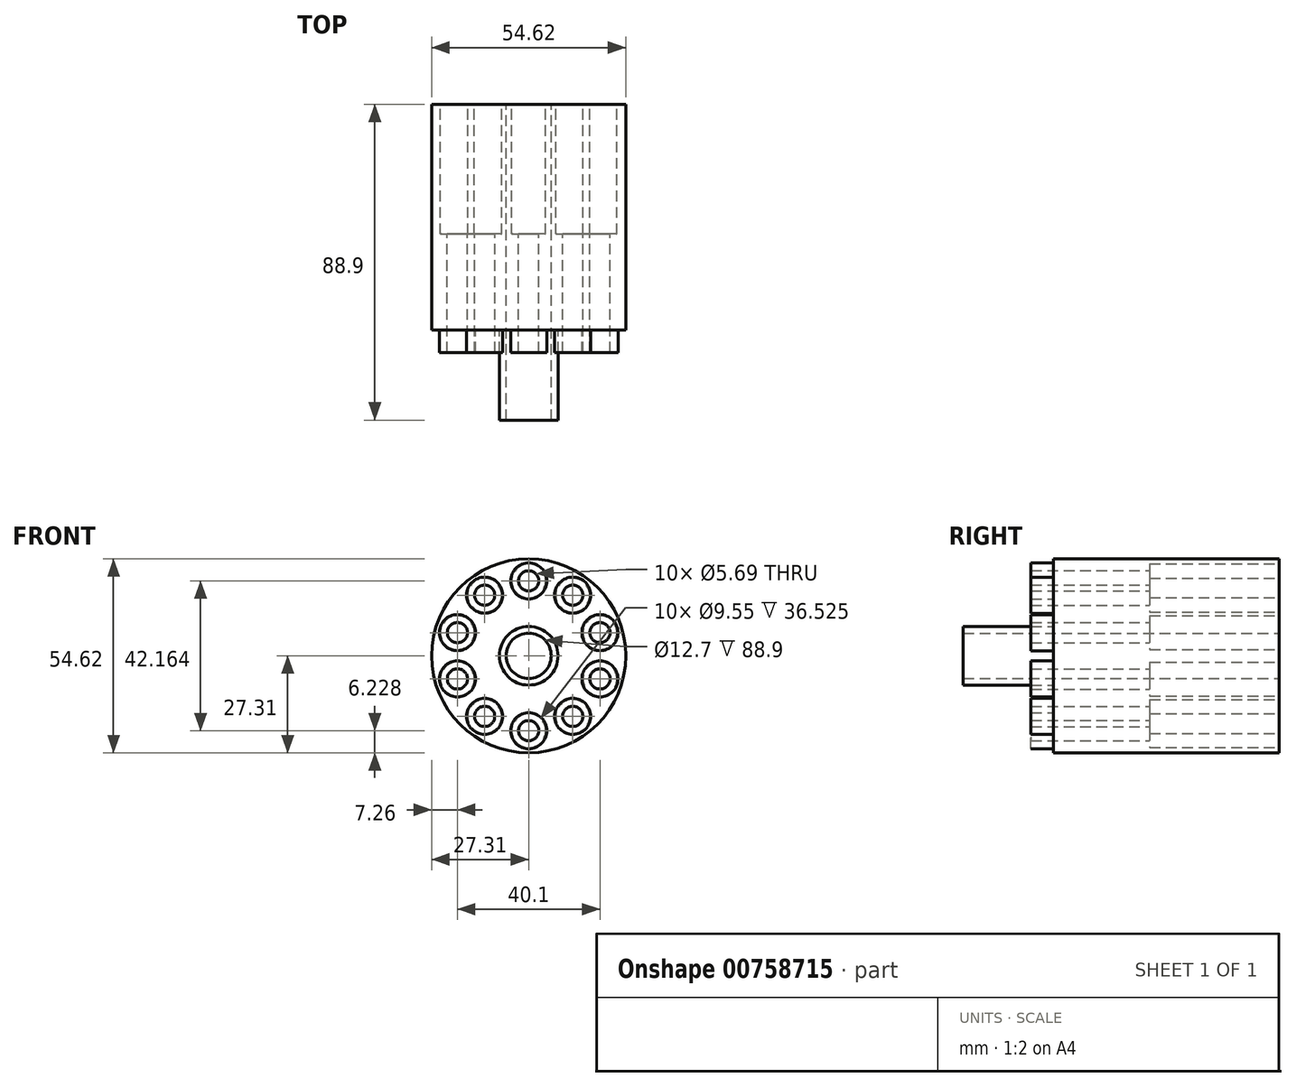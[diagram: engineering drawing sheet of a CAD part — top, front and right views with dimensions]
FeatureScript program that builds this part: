
annotation { "Feature Type Name" : "Feature", "Feature Type Description" : "" }
export const myFeature = defineFeature(function(context is Context, id is Id, definition is map)
    precondition{}
    {
        {
            var Q0;
            Q0=qCreatedBy(makeId("Front.planeOp"),FACE);
            var sketch = newSketch(context, id + "F0", { "sketchPlane" : qUnion([Q0])});
            skCircle(sketch, "E0", {"center": v(0, 0) * mm, "radius": 27.3 * mm});
            skSolve(sketch);
        }
        {
            var Q0;
            Q0 = qSketchRegion(id + "F0", true);
            extrude(context, id + "F1", {"entities" : qUnion([Q0]), "depth" : 63.5 * mm, "offsetDistance" : 25.4 * mm});
        }
        {
            var Q0;
            Q0=makeQuery(id+"F1.opExtrude","CAP_FACE",FACE,{"disambiguationData":[OSD([sQuery(id+"F0.wireOp",EDGE,"E0")])],"isStart":true});
            var sketch = newSketch(context, id + "F2", { "sketchPlane" : qUnion([Q0])});
            skLineSegment(sketch, "E1", {"start": v(0, 0) * mm, "end": v(0, 21.08) * mm});
            skLineSegment(sketch, "E2", {"start": v(0, 0) * mm, "end": v(12.4, 17.06) * mm});
            skLineSegment(sketch, "E3", {"start": v(0, 0) * mm, "end": v(20.05, 6.51) * mm});
            skLineSegment(sketch, "E4", {"start": v(0, 0) * mm, "end": v(20.05, -6.51) * mm});
            skLineSegment(sketch, "E5", {"start": v(0, 0) * mm, "end": v(12.4, -17.06) * mm});
            skLineSegment(sketch, "E6", {"start": v(0, 0) * mm, "end": v(0, -21.08) * mm});
            skLineSegment(sketch, "E7", {"start": v(0, 0) * mm, "end": v(-20.05, -6.51) * mm});
            skLineSegment(sketch, "E8", {"start": v(0, 0) * mm, "end": v(-20.05, 6.51) * mm});
            skLineSegment(sketch, "E9", {"start": v(0, 0) * mm, "end": v(-12.4, 17.06) * mm});
            skLineSegment(sketch, "E10", {"start": v(0, 0) * mm, "end": v(-12.4, -17.06) * mm});
            skCircle(sketch, "E11", {"center": v(0, 21.08) * mm, "radius": 4.78 * mm});
            skCircle(sketch, "E12", {"center": v(12.4, 17.06) * mm, "radius": 4.78 * mm});
            skCircle(sketch, "E13", {"center": v(20.05, 6.51) * mm, "radius": 4.78 * mm});
            skCircle(sketch, "E14", {"center": v(20.05, -6.51) * mm, "radius": 4.78 * mm});
            skCircle(sketch, "E15", {"center": v(12.4, -17.06) * mm, "radius": 4.78 * mm});
            skCircle(sketch, "E16", {"center": v(0, -21.08) * mm, "radius": 4.78 * mm});
            skCircle(sketch, "E17", {"center": v(-12.4, -17.06) * mm, "radius": 4.78 * mm});
            skCircle(sketch, "E18", {"center": v(-20.05, -6.51) * mm, "radius": 4.78 * mm});
            skCircle(sketch, "E19", {"center": v(-20.05, 6.51) * mm, "radius": 4.78 * mm});
            skCircle(sketch, "E20", {"center": v(-12.4, 17.06) * mm, "radius": 4.78 * mm});
            skCircle(sketch, "E21", {"center": v(0, 21.08) * mm, "radius": 2.84 * mm});
            skCircle(sketch, "E22", {"center": v(12.4, 17.06) * mm, "radius": 2.84 * mm});
            skCircle(sketch, "E23", {"center": v(20.05, 6.51) * mm, "radius": 2.84 * mm});
            skCircle(sketch, "E24", {"center": v(20.05, -6.51) * mm, "radius": 2.84 * mm});
            skCircle(sketch, "E25", {"center": v(12.4, -17.06) * mm, "radius": 2.84 * mm});
            skCircle(sketch, "E26", {"center": v(0, -21.08) * mm, "radius": 2.84 * mm});
            skCircle(sketch, "E27", {"center": v(-12.4, -17.06) * mm, "radius": 2.84 * mm});
            skCircle(sketch, "E28", {"center": v(-20.05, -6.51) * mm, "radius": 2.84 * mm});
            skCircle(sketch, "E29", {"center": v(-20.05, 6.51) * mm, "radius": 2.84 * mm});
            skCircle(sketch, "E30", {"center": v(-12.4, 17.06) * mm, "radius": 2.84 * mm});
            skSolve(sketch);
        }
        {
            var Q0;
            Q0=makeQuery(id+"F2.imprint","IMPRINT",FACE,{"disambiguationData":[TD([[makeQuery(id+"F2.imprint","IMPRINT",EDGE,{"derivedFrom":sQuery(id+"F2.wireOp",EDGE,"E28")}),1.0]])]});
            var Q1;
            Q1=makeQuery(id+"F2.imprint","IMPRINT",FACE,{"disambiguationData":[TD([[makeQuery(id+"F2.imprint","IMPRINT",EDGE,{"derivedFrom":sQuery(id+"F2.wireOp",EDGE,"E29")}),1.0]])]});
            var Q2;
            Q2=makeQuery(id+"F2.imprint","IMPRINT",FACE,{"disambiguationData":[TD([[makeQuery(id+"F2.imprint","IMPRINT",EDGE,{"derivedFrom":sQuery(id+"F2.wireOp",EDGE,"E30")}),1.0]])]});
            var Q3;
            Q3=makeQuery(id+"F2.imprint","IMPRINT",FACE,{"disambiguationData":[TD([[makeQuery(id+"F2.imprint","IMPRINT",EDGE,{"derivedFrom":sQuery(id+"F2.wireOp",EDGE,"E21")}),1.0]])]});
            var Q4;
            Q4=makeQuery(id+"F2.imprint","IMPRINT",FACE,{"disambiguationData":[TD([[makeQuery(id+"F2.imprint","IMPRINT",EDGE,{"derivedFrom":sQuery(id+"F2.wireOp",EDGE,"E22")}),1.0]])]});
            var Q5;
            Q5=makeQuery(id+"F2.imprint","IMPRINT",FACE,{"disambiguationData":[TD([[makeQuery(id+"F2.imprint","IMPRINT",EDGE,{"derivedFrom":sQuery(id+"F2.wireOp",EDGE,"E23")}),1.0]])]});
            var Q6;
            Q6=makeQuery(id+"F2.imprint","IMPRINT",FACE,{"disambiguationData":[TD([[makeQuery(id+"F2.imprint","IMPRINT",EDGE,{"derivedFrom":sQuery(id+"F2.wireOp",EDGE,"E24")}),1.0]])]});
            var Q7;
            Q7=makeQuery(id+"F2.imprint","IMPRINT",FACE,{"disambiguationData":[TD([[makeQuery(id+"F2.imprint","IMPRINT",EDGE,{"derivedFrom":sQuery(id+"F2.wireOp",EDGE,"E25")}),1.0]])]});
            var Q8;
            Q8=makeQuery(id+"F2.imprint","IMPRINT",FACE,{"disambiguationData":[TD([[makeQuery(id+"F2.imprint","IMPRINT",EDGE,{"derivedFrom":sQuery(id+"F2.wireOp",EDGE,"E26")}),1.0]])]});
            var Q9;
            Q9=makeQuery(id+"F2.imprint","IMPRINT",FACE,{"disambiguationData":[TD([[makeQuery(id+"F2.imprint","IMPRINT",EDGE,{"derivedFrom":sQuery(id+"F2.wireOp",EDGE,"E27")}),1.0]])]});
            extrude(context, id + "F3", {"entities" : qUnion([Q0, Q1, Q2, Q3, Q4, Q5, Q6, Q7, Q8, Q9]), "operationType" : NewBodyOperationType.REMOVE, "oppositeDirection" : true, "depth" : 86.61 * mm, "offsetDistance" : 25.4 * mm});
        }
        {
            var Q0;
            Q0=makeQuery(id+"F1.opExtrude","CAP_FACE",FACE,{"disambiguationData":[OSD([sQuery(id+"F0.wireOp",EDGE,"E0")])],"isStart":false});
            var sketch = newSketch(context, id + "F4", { "sketchPlane" : qUnion([Q0])});
            skCircle(sketch, "E31", {"center": v(-12.4, 17.06) * mm, "radius": 5.08 * mm});
            skCircle(sketch, "E32", {"center": v(0, 21.08) * mm, "radius": 5.08 * mm});
            skCircle(sketch, "E33", {"center": v(12.4, 17.06) * mm, "radius": 5.08 * mm});
            skCircle(sketch, "E34", {"center": v(20.05, 6.51) * mm, "radius": 5.08 * mm});
            skCircle(sketch, "E35", {"center": v(20.05, -6.51) * mm, "radius": 5.08 * mm});
            skCircle(sketch, "E36", {"center": v(12.4, -17.06) * mm, "radius": 5.08 * mm});
            skCircle(sketch, "E37", {"center": v(0, -21.08) * mm, "radius": 5.08 * mm});
            skCircle(sketch, "E38", {"center": v(-12.4, -17.06) * mm, "radius": 5.08 * mm});
            skCircle(sketch, "E39", {"center": v(-20.05, -6.51) * mm, "radius": 5.08 * mm});
            skCircle(sketch, "E40", {"center": v(-20.05, 6.51) * mm, "radius": 5.08 * mm});
            skSolve(sketch);
        }
        {
            var Q0;
            Q0=makeQuery(id+"F4.imprint","IMPRINT",FACE,{"disambiguationData":[TD([[makeQuery(id+"F4.imprint","IMPRINT",EDGE,{"derivedFrom":sQuery(id+"F4.wireOp",EDGE,"E32")}),1.0]])]});
            var Q1;
            Q1=makeQuery(id+"F4.imprint","IMPRINT",FACE,{"disambiguationData":[TD([[makeQuery(id+"F4.imprint","IMPRINT",EDGE,{"derivedFrom":sQuery(id+"F4.wireOp",EDGE,"E33")}),1.0]])]});
            var Q2;
            Q2=makeQuery(id+"F4.imprint","IMPRINT",FACE,{"disambiguationData":[TD([[makeQuery(id+"F4.imprint","IMPRINT",EDGE,{"derivedFrom":sQuery(id+"F4.wireOp",EDGE,"E34")}),1.0]])]});
            var Q3;
            Q3=makeQuery(id+"F4.imprint","IMPRINT",FACE,{"disambiguationData":[TD([[makeQuery(id+"F4.imprint","IMPRINT",EDGE,{"derivedFrom":sQuery(id+"F4.wireOp",EDGE,"E35")}),1.0]])]});
            var Q4;
            Q4=makeQuery(id+"F4.imprint","IMPRINT",FACE,{"disambiguationData":[TD([[makeQuery(id+"F4.imprint","IMPRINT",EDGE,{"derivedFrom":sQuery(id+"F4.wireOp",EDGE,"E36")}),1.0]])]});
            var Q5;
            Q5=makeQuery(id+"F4.imprint","IMPRINT",FACE,{"disambiguationData":[TD([[makeQuery(id+"F4.imprint","IMPRINT",EDGE,{"derivedFrom":sQuery(id+"F4.wireOp",EDGE,"E37")}),1.0]])]});
            var Q6;
            Q6=makeQuery(id+"F4.imprint","IMPRINT",FACE,{"disambiguationData":[TD([[makeQuery(id+"F4.imprint","IMPRINT",EDGE,{"derivedFrom":sQuery(id+"F4.wireOp",EDGE,"E38")}),1.0]])]});
            var Q7;
            Q7=makeQuery(id+"F4.imprint","IMPRINT",FACE,{"disambiguationData":[TD([[makeQuery(id+"F4.imprint","IMPRINT",EDGE,{"derivedFrom":sQuery(id+"F4.wireOp",EDGE,"E39")}),1.0]])]});
            var Q8;
            Q8=makeQuery(id+"F4.imprint","IMPRINT",FACE,{"disambiguationData":[TD([[makeQuery(id+"F4.imprint","IMPRINT",EDGE,{"derivedFrom":sQuery(id+"F4.wireOp",EDGE,"E40")}),1.0]])]});
            var Q9;
            Q9=makeQuery(id+"F4.imprint","IMPRINT",FACE,{"disambiguationData":[TD([[makeQuery(id+"F4.imprint","IMPRINT",EDGE,{"derivedFrom":sQuery(id+"F4.wireOp",EDGE,"E31")}),1.0]])]});
            extrude(context, id + "F5", {"entities" : qUnion([Q0, Q1, Q2, Q3, Q4, Q5, Q6, Q7, Q8, Q9]), "operationType" : NewBodyOperationType.ADD, "depth" : 6.35 * mm, "offsetDistance" : 25.4 * mm});
        }
        {
            var Q0;
            Q0=makeQuery(id+"F1.opExtrude","CAP_FACE",FACE,{"disambiguationData":[OSD([sQuery(id+"F0.wireOp",EDGE,"E0")])],"isStart":false});
            var sketch = newSketch(context, id + "F6", { "sketchPlane" : qUnion([Q0])});
            skCircle(sketch, "E41", {"center": v(0, 0) * mm, "radius": 8.26 * mm});
            skCircle(sketch, "E42", {"center": v(0, 0) * mm, "radius": 6.35 * mm});
            skSolve(sketch);
        }
        {
            var Q0;
            Q0=makeQuery(id+"F6.imprint","IMPRINT",FACE,{"disambiguationData":[TD([[makeQuery(id+"F6.imprint","IMPRINT",EDGE,{"derivedFrom":sQuery(id+"F6.wireOp",EDGE,"E41")}),1.0]])]});
            extrude(context, id + "F7", {"entities" : qUnion([Q0]), "operationType" : NewBodyOperationType.ADD, "depth" : 25.4 * mm, "offsetDistance" : 25.4 * mm});
        }
        {
            var Q0;
            Q0=makeQuery(id+"F2.imprint","IMPRINT",FACE,{"disambiguationData":[TD([[makeQuery(id+"F2.imprint","IMPRINT",EDGE,{"derivedFrom":sQuery(id+"F2.wireOp",EDGE,"E20")}),1.0]])]});
            var Q1;
            Q1=makeQuery(id+"F2.imprint","IMPRINT",FACE,{"disambiguationData":[TD([[makeQuery(id+"F2.imprint","IMPRINT",EDGE,{"derivedFrom":sQuery(id+"F2.wireOp",EDGE,"E11")}),1.0]])]});
            var Q2;
            Q2=makeQuery(id+"F2.imprint","IMPRINT",FACE,{"disambiguationData":[TD([[makeQuery(id+"F2.imprint","IMPRINT",EDGE,{"derivedFrom":sQuery(id+"F2.wireOp",EDGE,"E12")}),1.0]])]});
            var Q3;
            Q3=makeQuery(id+"F2.imprint","IMPRINT",FACE,{"disambiguationData":[TD([[makeQuery(id+"F2.imprint","IMPRINT",EDGE,{"derivedFrom":sQuery(id+"F2.wireOp",EDGE,"E13")}),1.0]])]});
            var Q4;
            Q4=makeQuery(id+"F2.imprint","IMPRINT",FACE,{"disambiguationData":[TD([[makeQuery(id+"F2.imprint","IMPRINT",EDGE,{"derivedFrom":sQuery(id+"F2.wireOp",EDGE,"E14")}),1.0]])]});
            var Q5;
            Q5=makeQuery(id+"F2.imprint","IMPRINT",FACE,{"disambiguationData":[TD([[makeQuery(id+"F2.imprint","IMPRINT",EDGE,{"derivedFrom":sQuery(id+"F2.wireOp",EDGE,"E15")}),1.0]])]});
            var Q6;
            Q6=makeQuery(id+"F2.imprint","IMPRINT",FACE,{"disambiguationData":[TD([[makeQuery(id+"F2.imprint","IMPRINT",EDGE,{"derivedFrom":sQuery(id+"F2.wireOp",EDGE,"E16")}),1.0]])]});
            var Q7;
            Q7=makeQuery(id+"F2.imprint","IMPRINT",FACE,{"disambiguationData":[TD([[makeQuery(id+"F2.imprint","IMPRINT",EDGE,{"derivedFrom":sQuery(id+"F2.wireOp",EDGE,"E17")}),1.0]])]});
            var Q8;
            Q8=makeQuery(id+"F2.imprint","IMPRINT",FACE,{"disambiguationData":[TD([[makeQuery(id+"F2.imprint","IMPRINT",EDGE,{"derivedFrom":sQuery(id+"F2.wireOp",EDGE,"E18")}),1.0]])]});
            var Q9;
            Q9=makeQuery(id+"F2.imprint","IMPRINT",FACE,{"disambiguationData":[TD([[makeQuery(id+"F2.imprint","IMPRINT",EDGE,{"derivedFrom":sQuery(id+"F2.wireOp",EDGE,"E19")}),1.0]])]});
            extrude(context, id + "F8", {"entities" : qUnion([Q0, Q1, Q2, Q3, Q4, Q5, Q6, Q7, Q8, Q9]), "operationType" : NewBodyOperationType.REMOVE, "oppositeDirection" : true, "depth" : 36.53 * mm, "offsetDistance" : 25.4 * mm});
        }
        {
            var Q0;
            Q0=makeQuery(id+"F7.boolean.opBoolean","SPLIT",FACE,{"disambiguationData":[TD([makeQuery(id+"F7.opExtrude","SWEPT_FACE",FACE,{"disambiguationData":[OSD([sQuery(id+"F6.wireOp",EDGE,"E42")])]})])],"derivedFrom":makeQuery(id+"F1.opExtrude","CAP_FACE",FACE,{"disambiguationData":[OSD([sQuery(id+"F0.wireOp",EDGE,"E0")])],"isStart":false})});
            extrude(context, id + "F9", {"entities" : qUnion([Q0]), "operationType" : NewBodyOperationType.REMOVE, "oppositeDirection" : true, "depth" : 133.35 * mm, "offsetDistance" : 25.4 * mm});
        }
    });
